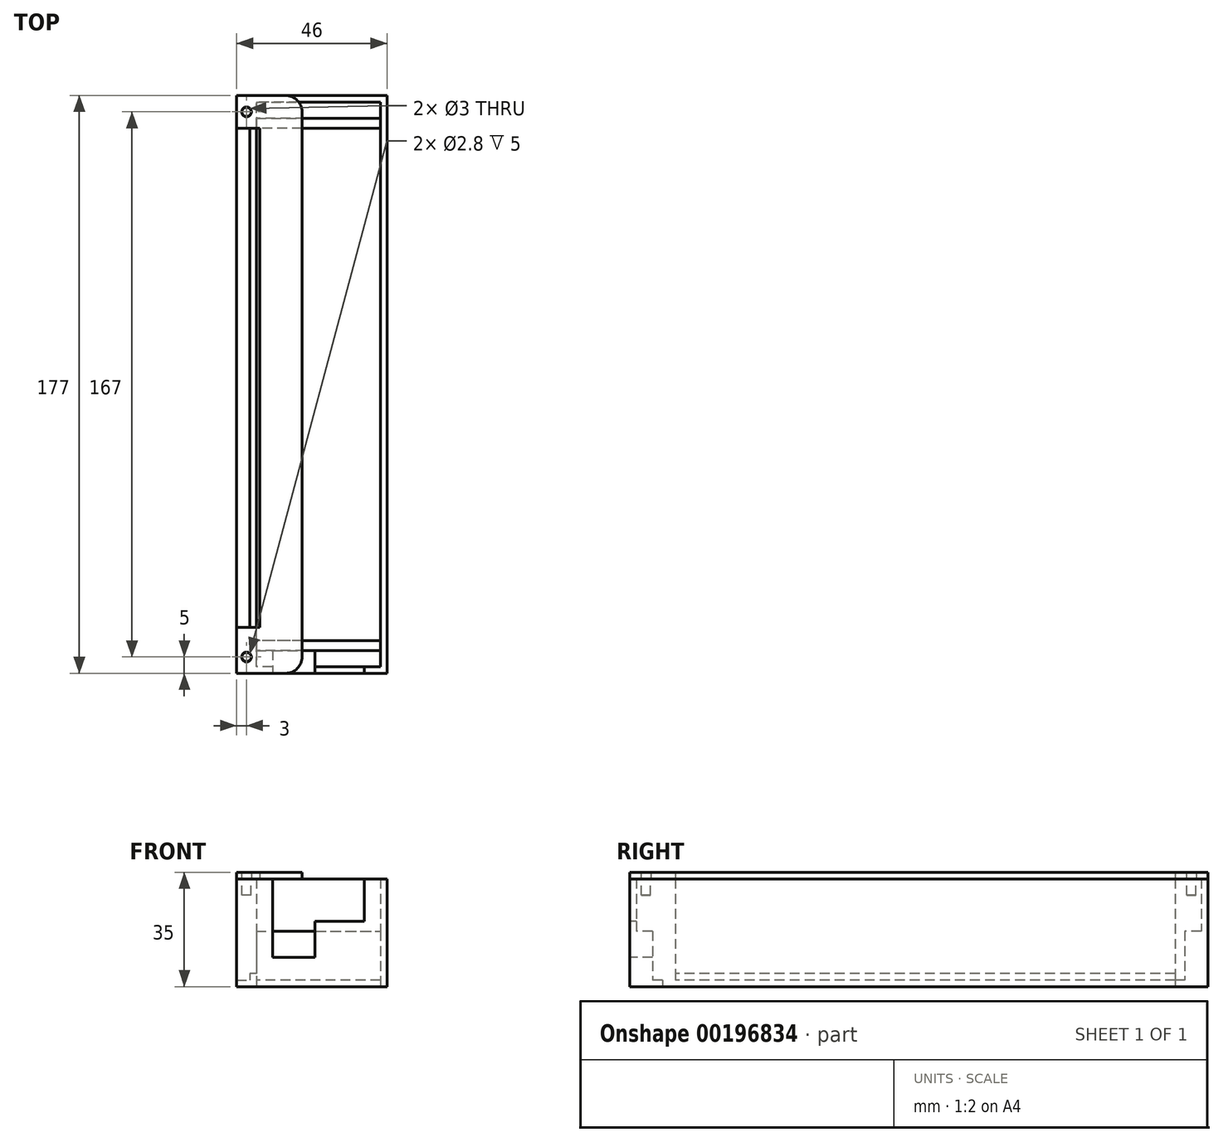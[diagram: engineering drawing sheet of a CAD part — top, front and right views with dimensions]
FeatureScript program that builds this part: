
annotation { "Feature Type Name" : "Feature", "Feature Type Description" : "" }
export const myFeature = defineFeature(function(context is Context, id is Id, definition is map)
    precondition{}
    {
        {
            var Q0;
            Q0=qCreatedBy(makeId("Top.planeOp"),FACE);
            var sketch = newSketch(context, id + "F0", { "sketchPlane" : qUnion([Q0])});
            skPoint(sketch, "E0.middle", {"position": v(0, 0) * mm});
            skLineSegment(sketch, "E1.bottom", {"start": v(19, -86.5) * mm, "end": v(-19, -86.5) * mm});
            skLineSegment(sketch, "E1.top", {"start": v(19, 86.5) * mm, "end": v(-19, 86.5) * mm});
            skLineSegment(sketch, "E1.left", {"start": v(19, -86.5) * mm, "end": v(19, 86.5) * mm});
            skLineSegment(sketch, "E1.right", {"start": v(-19, -86.5) * mm, "end": v(-19, 86.5) * mm});
            skLineSegment(sketch, "E2.bottom", {"start": v(-21, 88.5) * mm, "end": v(21, 88.5) * mm});
            skLineSegment(sketch, "E2.top", {"start": v(-21, -88.5) * mm, "end": v(21, -88.5) * mm});
            skLineSegment(sketch, "E2.left", {"start": v(-21, 88.5) * mm, "end": v(-21, -88.5) * mm});
            skLineSegment(sketch, "E2.right", {"start": v(21, 88.5) * mm, "end": v(21, -88.5) * mm});
            skSolve(sketch);
        }
        {
            var Q0;
            Q0 = qSketchRegion(id + "F0", true);
            extrude(context, id + "F1", {"entities" : qUnion([Q0]), "depth" : 33 * mm});
        }
        {
            var Q0;
            Q0=makeQuery(id+"F1.opExtrude","SWEPT_FACE",FACE,{"disambiguationData":[OSD([sQuery(id+"F0.wireOp",EDGE,"E2.left")])]});
            var sketch = newSketch(context, id + "F2", { "sketchPlane" : qUnion([Q0])});
            skLineSegment(sketch, "E3.bottom", {"start": v(-78.5, 33) * mm, "end": v(74.5, 33) * mm});
            skLineSegment(sketch, "E3.top", {"start": v(-78.5, 4) * mm, "end": v(74.5, 4) * mm});
            skLineSegment(sketch, "E3.left", {"start": v(-78.5, 33) * mm, "end": v(-78.5, 4) * mm});
            skLineSegment(sketch, "E3.right", {"start": v(74.5, 33) * mm, "end": v(74.5, 4) * mm});
            skSolve(sketch);
        }
        {
            var Q0;
            Q0 = qSketchRegion(id + "F2", true);
            extrude(context, id + "F3", {"entities" : qUnion([Q0]), "operationType" : NewBodyOperationType.REMOVE, "oppositeDirection" : true, "depth" : 5.8 * mm});
        }
        {
            var Q0;
            Q0=qCreatedBy(makeId("Top.planeOp"),FACE);
            var sketch = newSketch(context, id + "F4", { "sketchPlane" : qUnion([Q0])});
            skLineSegment(sketch, "E4.bottom", {"start": v(-19, 86.5) * mm, "end": v(19, 86.5) * mm});
            skLineSegment(sketch, "E4.top", {"start": v(-19, 81.5) * mm, "end": v(19, 81.5) * mm});
            skLineSegment(sketch, "E4.left", {"start": v(-19, 86.5) * mm, "end": v(-19, 81.5) * mm});
            skLineSegment(sketch, "E4.right", {"start": v(19, 86.5) * mm, "end": v(19, 81.5) * mm});
            skLineSegment(sketch, "E5.bottom", {"start": v(-19, -81.5) * mm, "end": v(19, -81.5) * mm});
            skLineSegment(sketch, "E5.top", {"start": v(-19, -86.5) * mm, "end": v(19, -86.5) * mm});
            skLineSegment(sketch, "E5.left", {"start": v(-19, -81.5) * mm, "end": v(-19, -86.5) * mm});
            skLineSegment(sketch, "E5.right", {"start": v(19, -81.5) * mm, "end": v(19, -86.5) * mm});
            skSolve(sketch);
        }
        {
            var Q0;
            Q0 = qSketchRegion(id + "F4", true);
            extrude(context, id + "F5", {"entities" : qUnion([Q0]), "operationType" : NewBodyOperationType.ADD, "depth" : 17 * mm});
        }
        {
            var Q0;
            Q0=qCreatedBy(makeId("Top.planeOp"),FACE);
            var sketch = newSketch(context, id + "F6", { "sketchPlane" : qUnion([Q0])});
            skLineSegment(sketch, "E6.bottom", {"start": v(-21, 88.5) * mm, "end": v(-25, 88.5) * mm});
            skLineSegment(sketch, "E6.top", {"start": v(-21, -88.5) * mm, "end": v(-25, -88.5) * mm});
            skLineSegment(sketch, "E6.left", {"start": v(-21, 88.5) * mm, "end": v(-21, -88.5) * mm});
            skLineSegment(sketch, "E6.right", {"start": v(-25, 88.5) * mm, "end": v(-25, -88.5) * mm});
            skLineSegment(sketch, "E7.bottom", {"start": v(19, 81.5) * mm, "end": v(-19, 81.5) * mm});
            skLineSegment(sketch, "E7.top", {"start": v(19, 78.5) * mm, "end": v(-19, 78.5) * mm});
            skLineSegment(sketch, "E7.left", {"start": v(19, 81.5) * mm, "end": v(19, 78.5) * mm});
            skLineSegment(sketch, "E7.right", {"start": v(-19, 81.5) * mm, "end": v(-19, 78.5) * mm});
            skLineSegment(sketch, "E8.bottom", {"start": v(19, -78.5) * mm, "end": v(-19, -78.5) * mm});
            skLineSegment(sketch, "E8.top", {"start": v(19, -81.5) * mm, "end": v(-19, -81.5) * mm});
            skLineSegment(sketch, "E8.left", {"start": v(19, -78.5) * mm, "end": v(19, -81.5) * mm});
            skLineSegment(sketch, "E8.right", {"start": v(-19, -78.5) * mm, "end": v(-19, -81.5) * mm});
            skSolve(sketch);
        }
        {
            var Q0;
            Q0 = qSketchRegion(id + "F6", true);
            extrude(context, id + "F7", {"entities" : qUnion([Q0]), "operationType" : NewBodyOperationType.ADD, "depth" : 2 * mm});
        }
        {
            var Q0;
            Q0=makeQuery(id+"F7.opExtrude","CAP_FACE",FACE,{"disambiguationData":[OSD([sQuery(id+"F6.wireOp",EDGE,"E6.left"),sQuery(id+"F6.wireOp",EDGE,"E6.right"),sQuery(id+"F6.wireOp",EDGE,"f915Lq7b-FzUm-4MdD-j7i7-blN7QO3VrcIc.bottom"),sQuery(id+"F6.wireOp",EDGE,"f915Lq7b-FzUm-4MdD-j7i7-blN7QO3VrcIc.top"),sQuery(id+"F6.wireOp",EDGE,"f915Lq7b-FzUm-4MdD-j7i7-blN7QO3VrcIc.left"),sQuery(id+"F6.wireOp",EDGE,"f915Lq7b-FzUm-4MdD-j7i7-blN7QO3VrcIc.right"),sQuery(id+"F6.wireOp",EDGE,"4NsWTKod-1fxG-jes7-M88g-cuhNPlkVH1BH.bottom"),sQuery(id+"F6.wireOp",EDGE,"4NsWTKod-1fxG-jes7-M88g-cuhNPlkVH1BH.top"),sQuery(id+"F6.wireOp",EDGE,"4NsWTKod-1fxG-jes7-M88g-cuhNPlkVH1BH.left"),sQuery(id+"F6.wireOp",EDGE,"4NsWTKod-1fxG-jes7-M88g-cuhNPlkVH1BH.right")])],"isStart":false});
            var sketch = newSketch(context, id + "F8", { "sketchPlane" : qUnion([Q0])});
            skLineSegment(sketch, "E9.bottom", {"start": v(-21, -74.5) * mm, "end": v(-25, -74.5) * mm});
            skLineSegment(sketch, "E9.top", {"start": v(-21, -88.5) * mm, "end": v(-25, -88.5) * mm});
            skLineSegment(sketch, "E9.left", {"start": v(-21, -74.5) * mm, "end": v(-21, -88.5) * mm});
            skLineSegment(sketch, "E9.right", {"start": v(-25, -74.5) * mm, "end": v(-25, -88.5) * mm});
            skLineSegment(sketch, "E10.bottom", {"start": v(-25, 78.5) * mm, "end": v(-21, 78.5) * mm});
            skLineSegment(sketch, "E10.top", {"start": v(-25, 88.5) * mm, "end": v(-21, 88.5) * mm});
            skLineSegment(sketch, "E10.left", {"start": v(-25, 78.5) * mm, "end": v(-25, 88.5) * mm});
            skLineSegment(sketch, "E10.right", {"start": v(-21, 78.5) * mm, "end": v(-21, 88.5) * mm});
            skSolve(sketch);
        }
        {
            var Q0;
            Q0 = qSketchRegion(id + "F8", true);
            extrude(context, id + "F9", {"entities" : qUnion([Q0]), "operationType" : NewBodyOperationType.ADD, "depth" : 31 * mm});
        }
        {
            var Q0;
            {var subQ0=sQuery(id+"F0.wireOp",EDGE,"E2.left");var subQ1=sQuery(id+"F0.wireOp",EDGE,"E2.top");var subQ2=sQuery(id+"F0.wireOp",EDGE,"E1.right");var subQ3=sQuery(id+"F0.wireOp",EDGE,"E1.bottom");Q0=makeQuery(id+"F9.boolean.opBoolean","MERGE",FACE,{"derivedFrom":[makeQuery(id+"F3.boolean.opBoolean","SPLIT",FACE,{"disambiguationData":[TD([makeQuery(id+"F13.boolean.opBoolean","COPY",FACE,{"derivedFrom":makeQuery(id+"F13.opExtrude","SWEPT_FACE",FACE,{"disambiguationData":[OSD([sQuery(id+"F12.wireOp",EDGE,"E13.left")])]})})])],"derivedFrom":makeQuery(id+"F1.opExtrude","CAP_FACE",FACE,{"disambiguationData":[OSD([subQ3,sQuery(id+"F0.wireOp",EDGE,"E1.top"),sQuery(id+"F0.wireOp",EDGE,"E1.left"),subQ2,sQuery(id+"F0.wireOp",EDGE,"E2.bottom"),subQ1,subQ0,sQuery(id+"F0.wireOp",EDGE,"E2.right")])],"isStart":false})}),makeQuery(id+"F9.opExtrude","CAP_FACE",FACE,{"disambiguationData":[OSD([sQuery(id+"F8.wireOp",EDGE,"E9.bottom"),sQuery(id+"F8.wireOp",EDGE,"E9.top"),sQuery(id+"F8.wireOp",EDGE,"E9.left"),sQuery(id+"F8.wireOp",EDGE,"E9.right")])],"isStart":false})]});}
            var sketch = newSketch(context, id + "F10", { "sketchPlane" : qUnion([Q0])});
            skCircle(sketch, "E11", {"center": v(-22, -83.5) * mm, "radius": 1.4 * mm});
            skCircle(sketch, "E12", {"center": v(-22, 83.5) * mm, "radius": 1.4 * mm});
            skSolve(sketch);
        }
        {
            var Q0;
            Q0 = qSketchRegion(id + "F10", true);
            extrude(context, id + "F11", {"entities" : qUnion([Q0]), "operationType" : NewBodyOperationType.REMOVE, "oppositeDirection" : true, "depth" : 5 * mm});
        }
        {
            var Q0;
            Q0=makeQuery(id+"F1.opExtrude","SWEPT_FACE",FACE,{"disambiguationData":[OSD([sQuery(id+"F0.wireOp",EDGE,"E2.top")])]});
            var sketch = newSketch(context, id + "F12", { "sketchPlane" : qUnion([Q0])});
            skLineSegment(sketch, "E13.bottom", {"start": v(14, 33) * mm, "end": v(-14, 33) * mm});
            skLineSegment(sketch, "E13.top", {"start": v(-14, 20) * mm, "end": v(14, 20) * mm});
            skLineSegment(sketch, "E13.left", {"start": v(-14, 33) * mm, "end": v(-14, 20) * mm});
            skLineSegment(sketch, "E13.right", {"start": v(14, 33) * mm, "end": v(14, 20) * mm});
            skLineSegment(sketch, "E14.bottom", {"start": v(-14, 20) * mm, "end": v(-1, 20) * mm});
            skLineSegment(sketch, "E14.top", {"start": v(-14, 9) * mm, "end": v(-1, 9) * mm});
            skLineSegment(sketch, "E14.left", {"start": v(-14, 20) * mm, "end": v(-14, 9) * mm});
            skLineSegment(sketch, "E14.right", {"start": v(-1, 20) * mm, "end": v(-1, 9) * mm});
            skSolve(sketch);
        }
        {
            var Q0;
            Q0 = qSketchRegion(id + "F12", true);
            extrude(context, id + "F13", {"entities" : qUnion([Q0]), "operationType" : NewBodyOperationType.REMOVE, "oppositeDirection" : true, "depth" : 7 * mm});
        }
        {
            var Q0;
            Q0=qCreatedBy(makeId("Top.planeOp"),FACE);
            cPlane(context, id + "F14", {"entities" : qUnion([Q0]), "cplaneType" : CPlaneType.OFFSET, "offset" : 33 * mm, "width" : 150 * mm, "height" : 150 * mm});
        }
        {
            var Q0;
            Q0=qCreatedBy(id+"F14.planeOp",FACE);
            var sketch = newSketch(context, id + "F15", { "sketchPlane" : qUnion([Q0])});
            skLineSegment(sketch, "E15.bottom", {"start": v(-25, 88.5) * mm, "end": v(-10, 88.5) * mm});
            skLineSegment(sketch, "E15.left", {"start": v(-25, 88.5) * mm, "end": v(-25, 78.5) * mm});
            skLineSegment(sketch, "E15.right", {"start": v(-5, 83.5) * mm, "end": v(-5, 78.5) * mm});
            skLineSegment(sketch, "E16", {"start": v(-5, 78.5) * mm, "end": v(-25, 78.5) * mm});
            skLineSegment(sketch, "E17.bottom", {"start": v(-5, 78.5) * mm, "end": v(-18, 78.5) * mm});
            skLineSegment(sketch, "E17.top", {"start": v(-5, 63.5) * mm, "end": v(-18, 63.5) * mm});
            skLineSegment(sketch, "E17.left", {"start": v(-5, 78.5) * mm, "end": v(-5, 63.5) * mm});
            skLineSegment(sketch, "E17.right", {"start": v(-18, 78.5) * mm, "end": v(-18, 63.5) * mm});
            skCircle(sketch, "E18", {"center": v(-22, 83.5) * mm, "radius": 1.5 * mm});
            skPoint(sketch, "E18.centerSnap0", {"position": v(-25, 83.5) * mm});
            skLineSegment(sketch, "E19.bottom", {"start": v(-25, -88.5) * mm, "end": v(-10, -88.5) * mm});
            skLineSegment(sketch, "E19.top", {"start": v(-25, -74.5) * mm, "end": v(-5, -74.5) * mm});
            skLineSegment(sketch, "E19.left", {"start": v(-25, -88.5) * mm, "end": v(-25, -74.5) * mm});
            skLineSegment(sketch, "E19.right", {"start": v(-5, -83.5) * mm, "end": v(-5, -74.5) * mm});
            skLineSegment(sketch, "E20.bottom", {"start": v(-5, -74.5) * mm, "end": v(-18, -74.5) * mm});
            skLineSegment(sketch, "E20.top", {"start": v(-5, -59.5) * mm, "end": v(-18, -59.5) * mm});
            skLineSegment(sketch, "E20.left", {"start": v(-5, -74.5) * mm, "end": v(-5, -59.5) * mm});
            skLineSegment(sketch, "E20.right", {"start": v(-18, -74.5) * mm, "end": v(-18, -59.5) * mm});
            skCircle(sketch, "E21", {"center": v(-22, -83.5) * mm, "radius": 1.5 * mm});
            skLineSegment(sketch, "E22.left", {"start": v(-5, 63.5) * mm, "end": v(-5, -59.5) * mm});
            skLineSegment(sketch, "E22.right", {"start": v(-18, 63.5) * mm, "end": v(-18, -59.5) * mm});
            skPoint(sketch, "E23.visualSharp", {"position": v(-5, 88.5) * mm});
            skArc(sketch, "E23.filletArc", {"start": v(-5, 83.5) * mm, "mid": v(-6.46, 87.04) * mm, "end": v(-10, 88.5) * mm});
            skPoint(sketch, "E24.visualSharp", {"position": v(-5, -88.5) * mm});
            skArc(sketch, "E24.filletArc", {"start": v(-10, -88.5) * mm, "mid": v(-6.46, -87.04) * mm, "end": v(-5, -83.5) * mm});
            skSolve(sketch);
        }
        {
            var Q0;
            Q0 = qSketchRegion(id + "F15", true);
            extrude(context, id + "F16", {"entities" : qUnion([Q0]), "depth" : 2 * mm});
        }
    });
